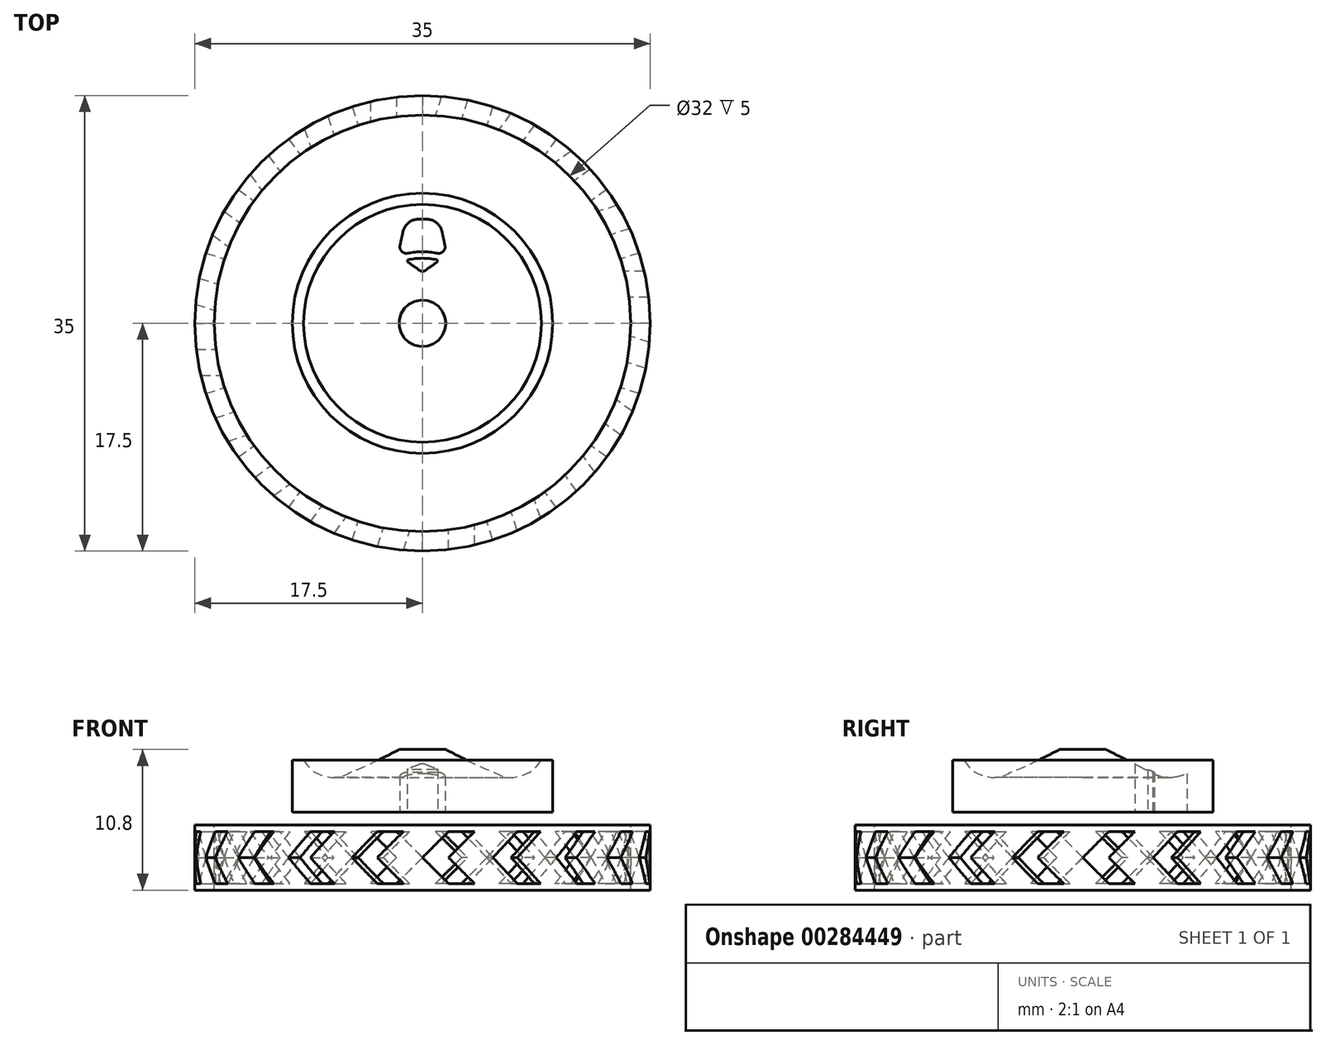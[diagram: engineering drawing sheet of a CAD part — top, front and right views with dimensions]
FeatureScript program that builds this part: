
annotation { "Feature Type Name" : "Feature", "Feature Type Description" : "" }
export const myFeature = defineFeature(function(context is Context, id is Id, definition is map)
    precondition{}
    {
        {
            var Q0;
            Q0=qCreatedBy(makeId("Front.planeOp"),FACE);
            var sketch = newSketch(context, id + "F0", { "sketchPlane" : qUnion([Q0])});
            skLineSegment(sketch, "E0", {"start": v(0, 0) * mm, "end": v(0, 44.58) * mm, "construction": true});
            skLineSegment(sketch, "E1", {"start": v(0, 44.58) * mm, "end": v(0, -44.8) * mm, "construction": true});
            skLineSegment(sketch, "E2", {"start": v(0, 0) * mm, "end": v(-63.75, 0) * mm, "construction": true});
            skLineSegment(sketch, "E3", {"start": v(-63.75, 0) * mm, "end": v(65.83, 0) * mm, "construction": true});
            skLineSegment(sketch, "E4.bottom", {"start": v(0, 7.5) * mm, "end": v(-17.5, 7.5) * mm});
            skLineSegment(sketch, "E4.top", {"start": v(0, -7.5) * mm, "end": v(-17.5, -7.5) * mm});
            skLineSegment(sketch, "E4.left", {"start": v(0, 7.5) * mm, "end": v(0, -7.5) * mm});
            skLineSegment(sketch, "E4.right", {"start": v(-17.5, 7.5) * mm, "end": v(-17.5, -7.5) * mm});
            skPoint(sketch, "E4.middle", {"position": v(-8.75, 0) * mm});
            skSolve(sketch);
        }
        {
            var Q0;
            Q0 = qSketchRegion(id + "F0", true);
            var Q1;
            Q1=sQuery(id+"F0.wireOp",EDGE,"E4.left");
            revolve(context, id + "F1", {"entities" : qUnion([Q0]), "axis" : qUnion([Q1]), "revolveType" : RevolveType.FULL});
        }
        {
            var Q0;
            Q0=makeQuery(id+"F1.opRevolve","SWEPT_EDGE",EDGE,{"disambiguationData":[OSD([sQuery(id+"F0.wireOp",EDGE,"E4.bottom"),sQuery(id+"F0.wireOp",EDGE,"E4.right")])]});
            var Q1;
            Q1=makeQuery(id+"F1.opRevolve","SWEPT_EDGE",EDGE,{"disambiguationData":[OSD([sQuery(id+"F0.wireOp",EDGE,"E4.top"),sQuery(id+"F0.wireOp",EDGE,"E4.right")])]});
            fillet(context, id + "F2", {"entities" : qUnion([Q0, Q1]), "radius" : 2.5 * mm, "tangentPropagation" : true, "allowEdgeOverflow" : false});
        }
        {
            var Q0;
            Q0=qCreatedBy(makeId("Right.planeOp"),FACE);
            var sketch = newSketch(context, id + "F3", { "sketchPlane" : qUnion([Q0])});
            skLineSegment(sketch, "E5", {"start": v(-15, 7.5) * mm, "end": v(-14.5, 7.5) * mm});
            skLineSegment(sketch, "E6", {"start": v(-17.5, 3) * mm, "end": v(-17.5, 5) * mm});
            skArc(sketch, "E7", {"start": v(-15, 7.5) * mm, "mid": v(-16.77, 6.77) * mm, "end": v(-17.5, 5) * mm});
            skLineSegment(sketch, "E8.0", {"start": v(-15, 6) * mm, "end": v(-14.5, 6) * mm});
            skLineSegment(sketch, "E9.0", {"start": v(-16, 3) * mm, "end": v(-16, 5) * mm});
            skArc(sketch, "E10.0", {"start": v(-15, 6) * mm, "mid": v(-15.7, 5.7) * mm, "end": v(-16, 5) * mm});
            skLineSegment(sketch, "E11", {"start": v(-14.5, 7.5) * mm, "end": v(-14.5, 6) * mm});
            skLineSegment(sketch, "E12", {"start": v(-16, 3) * mm, "end": v(-17.5, 3) * mm});
            skLineSegment(sketch, "E13", {"start": v(0, 0) * mm, "end": v(0, 13.46) * mm, "construction": true});
            skLineSegment(sketch, "E14", {"start": v(0, 13.46) * mm, "end": v(0, -5.77) * mm, "construction": true});
            skPoint(sketch, "E14.endSnap0", {"position": v(0, 6.73) * mm});
            skSolve(sketch);
        }
        {
            var Q0;
            Q0=makeQuery(id+"F3.imprint","IMPRINT",FACE,{"disambiguationData":[TD([[makeQuery(id+"F3.imprint","IMPRINT",EDGE,{"derivedFrom":sQuery(id+"F3.wireOp",EDGE,"E5")}),-1.0]])]});
            var Q1;
            Q1=sQuery(id+"F3.wireOp",EDGE,"E14");
            revolve(context, id + "F4", {"operationType" : NewBodyOperationType.REMOVE, "entities" : qUnion([Q0]), "axis" : qUnion([Q1]), "revolveType" : RevolveType.SYMMETRIC, "oppositeDirection" : true, "angle" : 5 * degree});
        }
        {
            var Q0;
            Q0=qCreatedBy(makeId("Front.planeOp"),FACE);
            var sketch = newSketch(context, id + "F5", { "sketchPlane" : qUnion([Q0])});
            skLineSegment(sketch, "E15", {"start": v(0, 0) * mm, "end": v(2, 2) * mm});
            skLineSegment(sketch, "E16", {"start": v(2, 2) * mm, "end": v(4, 2) * mm});
            skLineSegment(sketch, "E17", {"start": v(4, 2) * mm, "end": v(2, 0) * mm});
            skLineSegment(sketch, "E18.MirrorCS", {"start": v(4, -2) * mm, "end": v(2, 0) * mm});
            skLineSegment(sketch, "E19.MirrorCS", {"start": v(2, -2) * mm, "end": v(4, -2) * mm});
            skLineSegment(sketch, "E20.MirrorCS", {"start": v(0, 0) * mm, "end": v(2, -2) * mm});
            skSolve(sketch);
        }
        {
            var Q0;
            Q0 = qSketchRegion(id + "F5", true);
            extrude(context, id + "F6", {"entities" : qUnion([Q0]), "depth" : 25 * mm});
        }
        {
            var Q0;
            Q0=qCreatedBy(makeId("Front.planeOp"),FACE);
            var sketch = newSketch(context, id + "F7", { "sketchPlane" : qUnion([Q0])});
            skLineSegment(sketch, "E21", {"start": v(-17.5, -5) * mm, "end": v(-17.5, 5) * mm});
            skLineSegment(sketch, "E22.bottom", {"start": v(-16, 2.5) * mm, "end": v(-18, 2.5) * mm});
            skLineSegment(sketch, "E22.top", {"start": v(-16, -2.5) * mm, "end": v(-18, -2.5) * mm});
            skLineSegment(sketch, "E22.left", {"start": v(-16, 2.5) * mm, "end": v(-16, -2.5) * mm});
            skLineSegment(sketch, "E22.right", {"start": v(-18, 2.5) * mm, "end": v(-18, -2.5) * mm});
            skPoint(sketch, "E22.middle", {"position": v(-17, 0) * mm});
            skLineSegment(sketch, "E23", {"start": v(0, 0) * mm, "end": v(-29.9, 0) * mm, "construction": true});
            skLineSegment(sketch, "E24", {"start": v(-29.9, 0) * mm, "end": v(28.8, 0) * mm, "construction": true});
            skSolve(sketch);
        }
        {
            var Q0;
            Q0 = qSketchRegion(id + "F7", true);
            var Q1;
            Q1=sQuery(id+"F3.wireOp",EDGE,"E14");
            revolve(context, id + "F8", {"operationType" : NewBodyOperationType.INTERSECT, "entities" : qUnion([Q0]), "axis" : qUnion([Q1]), "revolveType" : RevolveType.FULL});
        }
        {
            var Q0;
            Q0=makeQuery(id+"F6.opExtrude","SWEPT_BODY",BODY,{"disambiguationData":[OSD([sQuery(id+"F5.wireOp",EDGE,"E15"),sQuery(id+"F5.wireOp",EDGE,"E16"),sQuery(id+"F5.wireOp",EDGE,"E17"),sQuery(id+"F5.wireOp",EDGE,"E18.MirrorCS"),sQuery(id+"F5.wireOp",EDGE,"E19.MirrorCS"),sQuery(id+"F5.wireOp",EDGE,"E20.MirrorCS")])]});
            var Q1;
            Q1=sQuery(id+"F3.wireOp",EDGE,"E14");
            circularPattern(context, id + "F9", {"entities" : qUnion([Q0]), "axis" : qUnion([Q1]), "angle" : 360 * degree, "instanceCount" : 20, "equalSpace" : true});
        }
        {
            var Q0;
            Q0=makeQuery(id+"F9.opPattern","COPY",BODY,{"derivedFrom":makeQuery(id+"F6.opExtrude","SWEPT_BODY",BODY,{"disambiguationData":[OSD([sQuery(id+"F5.wireOp",EDGE,"E15"),sQuery(id+"F5.wireOp",EDGE,"E16"),sQuery(id+"F5.wireOp",EDGE,"E17"),sQuery(id+"F5.wireOp",EDGE,"E18.MirrorCS"),sQuery(id+"F5.wireOp",EDGE,"E19.MirrorCS"),sQuery(id+"F5.wireOp",EDGE,"E20.MirrorCS")])]}),"instanceName":"1"});
            var Q1;
            Q1=makeQuery(id+"F9.opPattern","COPY",BODY,{"derivedFrom":makeQuery(id+"F6.opExtrude","SWEPT_BODY",BODY,{"disambiguationData":[OSD([sQuery(id+"F5.wireOp",EDGE,"E15"),sQuery(id+"F5.wireOp",EDGE,"E16"),sQuery(id+"F5.wireOp",EDGE,"E17"),sQuery(id+"F5.wireOp",EDGE,"E18.MirrorCS"),sQuery(id+"F5.wireOp",EDGE,"E19.MirrorCS"),sQuery(id+"F5.wireOp",EDGE,"E20.MirrorCS")])]}),"instanceName":"13"});
            var Q2;
            Q2=makeQuery(id+"F9.opPattern","COPY",BODY,{"derivedFrom":makeQuery(id+"F6.opExtrude","SWEPT_BODY",BODY,{"disambiguationData":[OSD([sQuery(id+"F5.wireOp",EDGE,"E15"),sQuery(id+"F5.wireOp",EDGE,"E16"),sQuery(id+"F5.wireOp",EDGE,"E17"),sQuery(id+"F5.wireOp",EDGE,"E18.MirrorCS"),sQuery(id+"F5.wireOp",EDGE,"E19.MirrorCS"),sQuery(id+"F5.wireOp",EDGE,"E20.MirrorCS")])]}),"instanceName":"12"});
            var Q3;
            Q3=makeQuery(id+"F6.opExtrude","SWEPT_BODY",BODY,{"disambiguationData":[OSD([sQuery(id+"F5.wireOp",EDGE,"E15"),sQuery(id+"F5.wireOp",EDGE,"E16"),sQuery(id+"F5.wireOp",EDGE,"E17"),sQuery(id+"F5.wireOp",EDGE,"E18.MirrorCS"),sQuery(id+"F5.wireOp",EDGE,"E19.MirrorCS"),sQuery(id+"F5.wireOp",EDGE,"E20.MirrorCS")])]});
            var Q4;
            Q4=makeQuery(id+"F9.opPattern","COPY",BODY,{"derivedFrom":makeQuery(id+"F6.opExtrude","SWEPT_BODY",BODY,{"disambiguationData":[OSD([sQuery(id+"F5.wireOp",EDGE,"E15"),sQuery(id+"F5.wireOp",EDGE,"E16"),sQuery(id+"F5.wireOp",EDGE,"E17"),sQuery(id+"F5.wireOp",EDGE,"E18.MirrorCS"),sQuery(id+"F5.wireOp",EDGE,"E19.MirrorCS"),sQuery(id+"F5.wireOp",EDGE,"E20.MirrorCS")])]}),"instanceName":"4"});
            var Q5;
            Q5=makeQuery(id+"F9.opPattern","COPY",BODY,{"derivedFrom":makeQuery(id+"F6.opExtrude","SWEPT_BODY",BODY,{"disambiguationData":[OSD([sQuery(id+"F5.wireOp",EDGE,"E15"),sQuery(id+"F5.wireOp",EDGE,"E16"),sQuery(id+"F5.wireOp",EDGE,"E17"),sQuery(id+"F5.wireOp",EDGE,"E18.MirrorCS"),sQuery(id+"F5.wireOp",EDGE,"E19.MirrorCS"),sQuery(id+"F5.wireOp",EDGE,"E20.MirrorCS")])]}),"instanceName":"11"});
            var Q6;
            Q6=makeQuery(id+"F9.opPattern","COPY",BODY,{"derivedFrom":makeQuery(id+"F6.opExtrude","SWEPT_BODY",BODY,{"disambiguationData":[OSD([sQuery(id+"F5.wireOp",EDGE,"E15"),sQuery(id+"F5.wireOp",EDGE,"E16"),sQuery(id+"F5.wireOp",EDGE,"E17"),sQuery(id+"F5.wireOp",EDGE,"E18.MirrorCS"),sQuery(id+"F5.wireOp",EDGE,"E19.MirrorCS"),sQuery(id+"F5.wireOp",EDGE,"E20.MirrorCS")])]}),"instanceName":"19"});
            var Q7;
            Q7=makeQuery(id+"F9.opPattern","COPY",BODY,{"derivedFrom":makeQuery(id+"F6.opExtrude","SWEPT_BODY",BODY,{"disambiguationData":[OSD([sQuery(id+"F5.wireOp",EDGE,"E15"),sQuery(id+"F5.wireOp",EDGE,"E16"),sQuery(id+"F5.wireOp",EDGE,"E17"),sQuery(id+"F5.wireOp",EDGE,"E18.MirrorCS"),sQuery(id+"F5.wireOp",EDGE,"E19.MirrorCS"),sQuery(id+"F5.wireOp",EDGE,"E20.MirrorCS")])]}),"instanceName":"15"});
            var Q8;
            Q8=makeQuery(id+"F9.opPattern","COPY",BODY,{"derivedFrom":makeQuery(id+"F6.opExtrude","SWEPT_BODY",BODY,{"disambiguationData":[OSD([sQuery(id+"F5.wireOp",EDGE,"E15"),sQuery(id+"F5.wireOp",EDGE,"E16"),sQuery(id+"F5.wireOp",EDGE,"E17"),sQuery(id+"F5.wireOp",EDGE,"E18.MirrorCS"),sQuery(id+"F5.wireOp",EDGE,"E19.MirrorCS"),sQuery(id+"F5.wireOp",EDGE,"E20.MirrorCS")])]}),"instanceName":"16"});
            var Q9;
            Q9=makeQuery(id+"F9.opPattern","COPY",BODY,{"derivedFrom":makeQuery(id+"F6.opExtrude","SWEPT_BODY",BODY,{"disambiguationData":[OSD([sQuery(id+"F5.wireOp",EDGE,"E15"),sQuery(id+"F5.wireOp",EDGE,"E16"),sQuery(id+"F5.wireOp",EDGE,"E17"),sQuery(id+"F5.wireOp",EDGE,"E18.MirrorCS"),sQuery(id+"F5.wireOp",EDGE,"E19.MirrorCS"),sQuery(id+"F5.wireOp",EDGE,"E20.MirrorCS")])]}),"instanceName":"18"});
            var Q10;
            Q10=makeQuery(id+"F9.opPattern","COPY",BODY,{"derivedFrom":makeQuery(id+"F6.opExtrude","SWEPT_BODY",BODY,{"disambiguationData":[OSD([sQuery(id+"F5.wireOp",EDGE,"E15"),sQuery(id+"F5.wireOp",EDGE,"E16"),sQuery(id+"F5.wireOp",EDGE,"E17"),sQuery(id+"F5.wireOp",EDGE,"E18.MirrorCS"),sQuery(id+"F5.wireOp",EDGE,"E19.MirrorCS"),sQuery(id+"F5.wireOp",EDGE,"E20.MirrorCS")])]}),"instanceName":"17"});
            var Q11;
            Q11=makeQuery(id+"F9.opPattern","COPY",BODY,{"derivedFrom":makeQuery(id+"F6.opExtrude","SWEPT_BODY",BODY,{"disambiguationData":[OSD([sQuery(id+"F5.wireOp",EDGE,"E15"),sQuery(id+"F5.wireOp",EDGE,"E16"),sQuery(id+"F5.wireOp",EDGE,"E17"),sQuery(id+"F5.wireOp",EDGE,"E18.MirrorCS"),sQuery(id+"F5.wireOp",EDGE,"E19.MirrorCS"),sQuery(id+"F5.wireOp",EDGE,"E20.MirrorCS")])]}),"instanceName":"3"});
            var Q12;
            Q12=makeQuery(id+"F9.opPattern","COPY",BODY,{"derivedFrom":makeQuery(id+"F6.opExtrude","SWEPT_BODY",BODY,{"disambiguationData":[OSD([sQuery(id+"F5.wireOp",EDGE,"E15"),sQuery(id+"F5.wireOp",EDGE,"E16"),sQuery(id+"F5.wireOp",EDGE,"E17"),sQuery(id+"F5.wireOp",EDGE,"E18.MirrorCS"),sQuery(id+"F5.wireOp",EDGE,"E19.MirrorCS"),sQuery(id+"F5.wireOp",EDGE,"E20.MirrorCS")])]}),"instanceName":"9"});
            var Q13;
            Q13=makeQuery(id+"F9.opPattern","COPY",BODY,{"derivedFrom":makeQuery(id+"F6.opExtrude","SWEPT_BODY",BODY,{"disambiguationData":[OSD([sQuery(id+"F5.wireOp",EDGE,"E15"),sQuery(id+"F5.wireOp",EDGE,"E16"),sQuery(id+"F5.wireOp",EDGE,"E17"),sQuery(id+"F5.wireOp",EDGE,"E18.MirrorCS"),sQuery(id+"F5.wireOp",EDGE,"E19.MirrorCS"),sQuery(id+"F5.wireOp",EDGE,"E20.MirrorCS")])]}),"instanceName":"5"});
            var Q14;
            Q14=makeQuery(id+"F9.opPattern","COPY",BODY,{"derivedFrom":makeQuery(id+"F6.opExtrude","SWEPT_BODY",BODY,{"disambiguationData":[OSD([sQuery(id+"F5.wireOp",EDGE,"E15"),sQuery(id+"F5.wireOp",EDGE,"E16"),sQuery(id+"F5.wireOp",EDGE,"E17"),sQuery(id+"F5.wireOp",EDGE,"E18.MirrorCS"),sQuery(id+"F5.wireOp",EDGE,"E19.MirrorCS"),sQuery(id+"F5.wireOp",EDGE,"E20.MirrorCS")])]}),"instanceName":"8"});
            var Q15;
            Q15=makeQuery(id+"F9.opPattern","COPY",BODY,{"derivedFrom":makeQuery(id+"F6.opExtrude","SWEPT_BODY",BODY,{"disambiguationData":[OSD([sQuery(id+"F5.wireOp",EDGE,"E15"),sQuery(id+"F5.wireOp",EDGE,"E16"),sQuery(id+"F5.wireOp",EDGE,"E17"),sQuery(id+"F5.wireOp",EDGE,"E18.MirrorCS"),sQuery(id+"F5.wireOp",EDGE,"E19.MirrorCS"),sQuery(id+"F5.wireOp",EDGE,"E20.MirrorCS")])]}),"instanceName":"2"});
            var Q16;
            Q16=makeQuery(id+"F9.opPattern","COPY",BODY,{"derivedFrom":makeQuery(id+"F6.opExtrude","SWEPT_BODY",BODY,{"disambiguationData":[OSD([sQuery(id+"F5.wireOp",EDGE,"E15"),sQuery(id+"F5.wireOp",EDGE,"E16"),sQuery(id+"F5.wireOp",EDGE,"E17"),sQuery(id+"F5.wireOp",EDGE,"E18.MirrorCS"),sQuery(id+"F5.wireOp",EDGE,"E19.MirrorCS"),sQuery(id+"F5.wireOp",EDGE,"E20.MirrorCS")])]}),"instanceName":"10"});
            var Q17;
            Q17=makeQuery(id+"F9.opPattern","COPY",BODY,{"derivedFrom":makeQuery(id+"F6.opExtrude","SWEPT_BODY",BODY,{"disambiguationData":[OSD([sQuery(id+"F5.wireOp",EDGE,"E15"),sQuery(id+"F5.wireOp",EDGE,"E16"),sQuery(id+"F5.wireOp",EDGE,"E17"),sQuery(id+"F5.wireOp",EDGE,"E18.MirrorCS"),sQuery(id+"F5.wireOp",EDGE,"E19.MirrorCS"),sQuery(id+"F5.wireOp",EDGE,"E20.MirrorCS")])]}),"instanceName":"6"});
            var Q18;
            Q18=makeQuery(id+"F9.opPattern","COPY",BODY,{"derivedFrom":makeQuery(id+"F6.opExtrude","SWEPT_BODY",BODY,{"disambiguationData":[OSD([sQuery(id+"F5.wireOp",EDGE,"E15"),sQuery(id+"F5.wireOp",EDGE,"E16"),sQuery(id+"F5.wireOp",EDGE,"E17"),sQuery(id+"F5.wireOp",EDGE,"E18.MirrorCS"),sQuery(id+"F5.wireOp",EDGE,"E19.MirrorCS"),sQuery(id+"F5.wireOp",EDGE,"E20.MirrorCS")])]}),"instanceName":"14"});
            var Q19;
            Q19=makeQuery(id+"F9.opPattern","COPY",BODY,{"derivedFrom":makeQuery(id+"F6.opExtrude","SWEPT_BODY",BODY,{"disambiguationData":[OSD([sQuery(id+"F5.wireOp",EDGE,"E15"),sQuery(id+"F5.wireOp",EDGE,"E16"),sQuery(id+"F5.wireOp",EDGE,"E17"),sQuery(id+"F5.wireOp",EDGE,"E18.MirrorCS"),sQuery(id+"F5.wireOp",EDGE,"E19.MirrorCS"),sQuery(id+"F5.wireOp",EDGE,"E20.MirrorCS")])]}),"instanceName":"7"});
            var Q20;
            Q20=makeQuery(id+"F1.opRevolve","SWEPT_BODY",BODY,{"disambiguationData":[OSD([sQuery(id+"F0.wireOp",EDGE,"E4.bottom"),sQuery(id+"F0.wireOp",EDGE,"E4.top"),sQuery(id+"F0.wireOp",EDGE,"E4.left"),sQuery(id+"F0.wireOp",EDGE,"E4.right")])]});
            booleanBodies(context, id + "F10", {"operationType" : BooleanOperationType.SUBTRACTION, "tools" : qUnion([Q0, Q1, Q2, Q3, Q4, Q5, Q6, Q7, Q8, Q9, Q10, Q11, Q12, Q13, Q14, Q15, Q16, Q17, Q18, Q19]), "targets" : qUnion([Q20])});
        }
        {
            var Q0;
            Q0=qCreatedBy(makeId("Top.planeOp"),FACE);
            var sketch = newSketch(context, id + "F11", { "sketchPlane" : qUnion([Q0])});
            skCircle(sketch, "E25", {"center": v(0, 0) * mm, "radius": 10 * mm});
            skSolve(sketch);
        }
        {
            var Q0;
            Q0 = qSketchRegion(id + "F11", true);
            extrude(context, id + "F12", {"entities" : qUnion([Q0]), "operationType" : NewBodyOperationType.REMOVE, "endBound" : BoundingType.THROUGH_ALL, "depth" : 25 * mm, "hasSecondDirection" : true, "secondDirectionOppositeDirection" : true, "secondDirectionDepth" : 25 * mm});
        }
        {
            var Q0;
            Q0=qCreatedBy(makeId("Front.planeOp"),FACE);
            var sketch = newSketch(context, id + "F13", { "sketchPlane" : qUnion([Q0])});
            skLineSegment(sketch, "E26.0", {"start": v(10, 7.5) * mm, "end": v(-10, 7.5) * mm});
            skLineSegment(sketch, "E27", {"start": v(10, 7.5) * mm, "end": v(10, -7.5) * mm});
            skLineSegment(sketch, "E28", {"start": v(0, 0) * mm, "end": v(26.42, 0) * mm, "construction": true});
            skLineSegment(sketch, "E29", {"start": v(26.42, 0) * mm, "end": v(-24.32, 0) * mm, "construction": true});
            skLineSegment(sketch, "E30", {"start": v(0, 0) * mm, "end": v(0, 14.17) * mm, "construction": true});
            skLineSegment(sketch, "E31", {"start": v(0, 8.3) * mm, "end": v(1.8, 8.3) * mm});
            skLineSegment(sketch, "E32", {"start": v(0, 8.3) * mm, "end": v(0, 3.5) * mm});
            skLineSegment(sketch, "E33", {"start": v(0, 3.5) * mm, "end": v(13.3, 3.5) * mm});
            skFitSpline(sketch, "E34", {"points": [v(1.8, 8.3) * mm, v(5.46, 6.56) * mm, v(6.46, 6.17) * mm, v(7.74, 6.34) * mm, v(9.13, 7.5) * mm], "startDerivative": vector(26.08, -13.5) * mm, "endDerivative": vector(6.39, 9.86) * mm});
            skSolve(sketch);
        }
        {
            var Q0;
            {var subQ3=sQuery(id+"F13.wireOp",EDGE,"E26.0");var subQ5=sQuery(id+"F13.wireOp",EDGE,"E27");var subQ6=makeQuery(id+"F13.imprint","INTERSECT",VERTEX,{"derivedFrom":[subQ3,subQ5]});Q0=makeQuery(id+"F13.imprint","IMPRINT",FACE,{"disambiguationData":[TD([[makeQuery(id+"F13.imprint","IMPRINT",EDGE,{"disambiguationData":[TD([[subQ6,-1.0]])],"derivedFrom":subQ3}),1.0]])]});}
            var Q1;
            {var subQ5=sQuery(id+"F13.wireOp",EDGE,"E31");Q1=makeQuery(id+"F13.imprint","IMPRINT",FACE,{"disambiguationData":[TD([[makeQuery(id+"F13.imprint","IMPRINT",EDGE,{"derivedFrom":subQ5}),-1.0]])]});}
            var Q2;
            Q2=sQuery(id+"F3.wireOp",EDGE,"E14");
            revolve(context, id + "F14", {"entities" : qUnion([Q0, Q1]), "axis" : qUnion([Q2]), "revolveType" : RevolveType.FULL});
        }
        {
            var Q0;
            Q0=qCreatedBy(makeId("Top.planeOp"),FACE);
            var sketch = newSketch(context, id + "F15", { "sketchPlane" : qUnion([Q0])});
            skArc(sketch, "E35", {"start": v(1.13, 5.38) * mm, "mid": v(0, 5.5) * mm, "end": v(-1.13, 5.38) * mm});
            skArc(sketch, "E36", {"start": v(0.38, 8) * mm, "mid": v(0, 8) * mm, "end": v(-0.38, 8) * mm});
            skLineSegment(sketch, "E37", {"start": v(-1.5, 7.04) * mm, "end": v(-1.73, 5.97) * mm});
            skLineSegment(sketch, "E38", {"start": v(0, 0) * mm, "end": v(0, 13.12) * mm, "construction": true});
            skLineSegment(sketch, "E39", {"start": v(0, 13.12) * mm, "end": v(0, -12.28) * mm, "construction": true});
            skLineSegment(sketch, "E40.MirrorCS", {"start": v(1.5, 7.04) * mm, "end": v(1.73, 5.97) * mm});
            skPoint(sketch, "E41.visualSharp", {"position": v(-1.32, 7.9) * mm});
            skArc(sketch, "E41.filletArc", {"start": v(-0.38, 8) * mm, "mid": v(-1.1, 7.7) * mm, "end": v(-1.5, 7.04) * mm});
            skPoint(sketch, "E42.visualSharp", {"position": v(1.32, 7.9) * mm});
            skArc(sketch, "E42.filletArc", {"start": v(1.5, 7.04) * mm, "mid": v(1.1, 7.7) * mm, "end": v(0.38, 8) * mm});
            skPoint(sketch, "E43.visualSharp", {"position": v(-1.9, 5.16) * mm});
            skArc(sketch, "E43.filletArc", {"start": v(-1.73, 5.97) * mm, "mid": v(-1.6, 5.52) * mm, "end": v(-1.13, 5.38) * mm});
            skPoint(sketch, "E44.visualSharp", {"position": v(1.9, 5.16) * mm});
            skArc(sketch, "E44.filletArc", {"start": v(1.13, 5.38) * mm, "mid": v(1.6, 5.52) * mm, "end": v(1.73, 5.97) * mm});
            skSolve(sketch);
        }
        {
            var Q0;
            Q0 = qSketchRegion(id + "F15", true);
            extrude(context, id + "F16", {"entities" : qUnion([Q0]), "operationType" : NewBodyOperationType.REMOVE, "endBound" : BoundingType.THROUGH_ALL, "depth" : 25 * mm});
        }
        {
            var Q0;
            Q0=qCreatedBy(makeId("Top.planeOp"),FACE);
            var sketch = newSketch(context, id + "F17", { "sketchPlane" : qUnion([Q0])});
            skArc(sketch, "E45", {"start": v(1.08, 4.88) * mm, "mid": v(0, 5) * mm, "end": v(-1.08, 4.88) * mm});
            skArc(sketch, "E46", {"start": v(0, 4) * mm, "mid": v(0, 4) * mm, "end": v(0, 4) * mm});
            skLineSegment(sketch, "E47", {"start": v(-1.12, 4.7) * mm, "end": v(-0.24, 4.07) * mm});
            skLineSegment(sketch, "E48.MirrorCS", {"start": v(1.12, 4.7) * mm, "end": v(0.24, 4.07) * mm});
            skPoint(sketch, "E49.visualSharp", {"position": v(-1.3, 4.83) * mm});
            skArc(sketch, "E49.filletArc", {"start": v(-1.08, 4.88) * mm, "mid": v(-1.16, 4.8) * mm, "end": v(-1.12, 4.7) * mm});
            skPoint(sketch, "E50.visualSharp", {"position": v(1.3, 4.83) * mm});
            skArc(sketch, "E50.filletArc", {"start": v(1.12, 4.7) * mm, "mid": v(1.16, 4.8) * mm, "end": v(1.08, 4.88) * mm});
            skPoint(sketch, "E51.visualSharp", {"position": v(-0.13, 4) * mm});
            skArc(sketch, "E51.filletArc", {"start": v(-0.24, 4.07) * mm, "mid": v(-0.13, 4.02) * mm, "end": v(0, 4) * mm});
            skPoint(sketch, "E52.visualSharp", {"position": v(0.13, 4) * mm});
            skArc(sketch, "E52.filletArc", {"start": v(0, 4) * mm, "mid": v(0.13, 4.02) * mm, "end": v(0.24, 4.07) * mm});
            skSolve(sketch);
        }
        {
            var Q0;
            Q0 = qSketchRegion(id + "F17", true);
            extrude(context, id + "F18", {"entities" : qUnion([Q0]), "operationType" : NewBodyOperationType.REMOVE, "endBound" : BoundingType.THROUGH_ALL, "depth" : 25 * mm});
        }
    });
